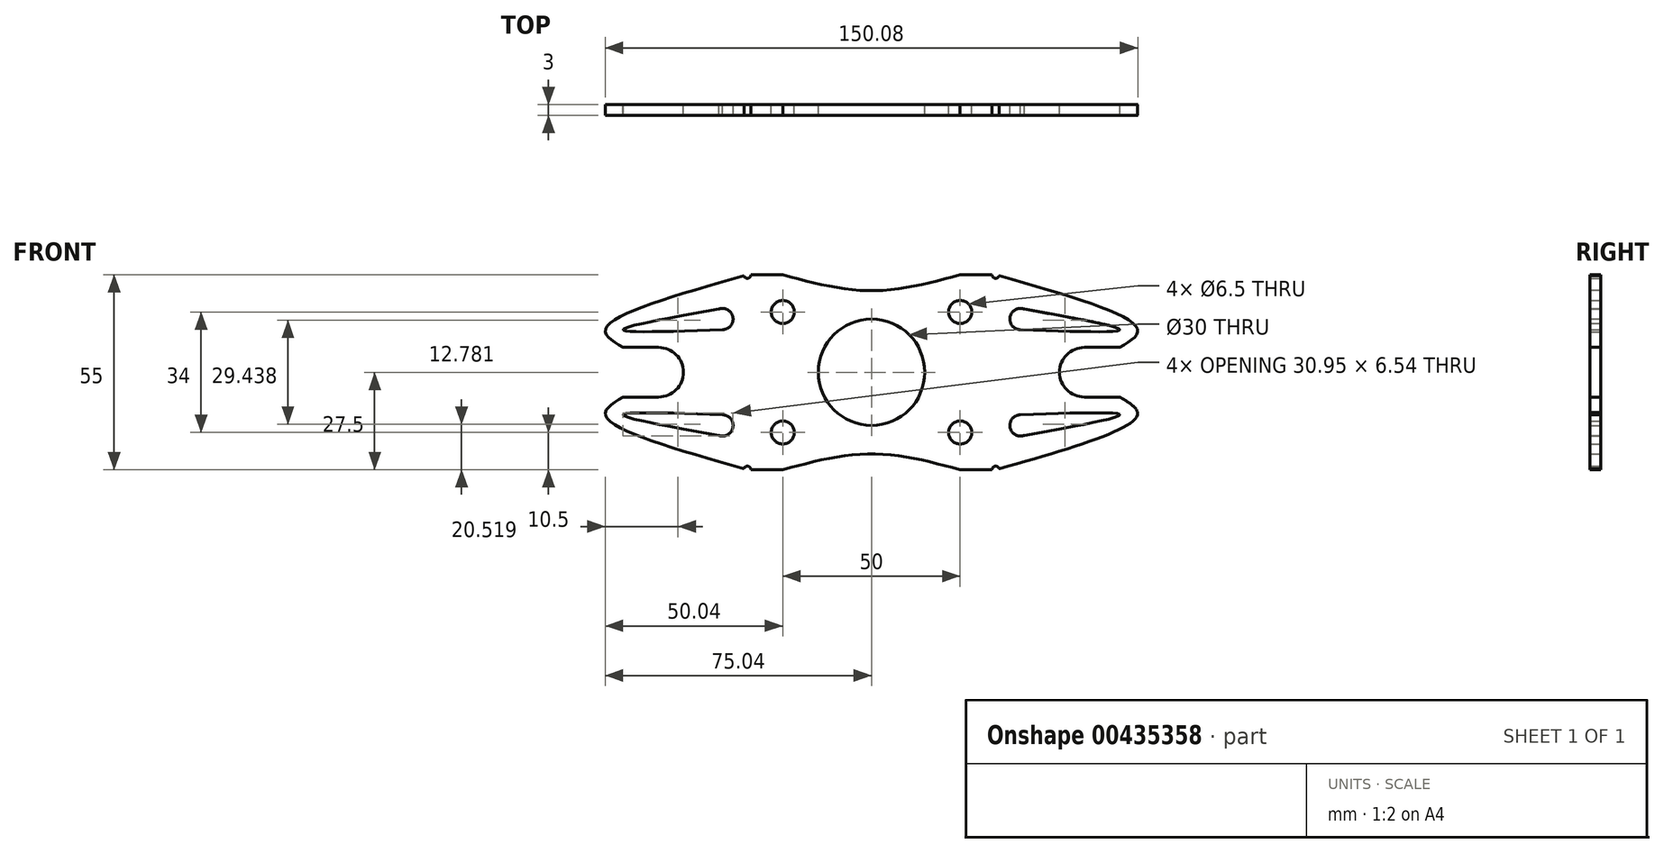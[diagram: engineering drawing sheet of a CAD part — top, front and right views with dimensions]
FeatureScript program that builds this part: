
annotation { "Feature Type Name" : "Feature", "Feature Type Description" : "" }
export const myFeature = defineFeature(function(context is Context, id is Id, definition is map)
    precondition{}
    {
        {
            var Q0;
            Q0=qCreatedBy(makeId("Front.planeOp"),FACE);
            var sketch = newSketch(context, id + "F0", { "sketchPlane" : qUnion([Q0])});
            skCircle(sketch, "E0", {"center": v(0, 0) * mm, "radius": 15 * mm});
            skLineSegment(sketch, "E1", {"start": v(-35, 26.5) * mm, "end": v(-35, 27.5) * mm});
            skLineSegment(sketch, "E2", {"start": v(-35, 27.5) * mm, "end": v(-35, 26.5) * mm});
            skLineSegment(sketch, "E3", {"start": v(-35, -27.5) * mm, "end": v(-25, -27.5) * mm});
            skLineSegment(sketch, "E4", {"start": v(35, -27.5) * mm, "end": v(35, -26.5) * mm});
            skLineSegment(sketch, "E5", {"start": v(35, 27.5) * mm, "end": v(25, 27.5) * mm});
            skLineSegment(sketch, "E6", {"start": v(25, 20.25) * mm, "end": v(25, 13.75) * mm});
            skLineSegment(sketch, "E7", {"start": v(-25, -20.25) * mm, "end": v(-25, -13.75) * mm});
            skLineSegment(sketch, "E8", {"start": v(25, 13.75) * mm, "end": v(25, 17) * mm});
            skLineSegment(sketch, "E9", {"start": v(25, 17) * mm, "end": v(25, 13.75) * mm});
            skArc(sketch, "E10", {"start": v(-60, -7) * mm, "mid": v(-53, 0) * mm, "end": v(-60, 7) * mm});
            skArc(sketch, "E11", {"start": v(60, 7) * mm, "mid": v(53, 0) * mm, "end": v(60, -7) * mm});
            skCircle(sketch, "E12", {"center": v(-25, 17) * mm, "radius": 3.25 * mm});
            skCircle(sketch, "E13", {"center": v(25, 17) * mm, "radius": 3.25 * mm});
            skCircle(sketch, "E14", {"center": v(25, -17) * mm, "radius": 3.25 * mm});
            skCircle(sketch, "E15", {"center": v(-25, -17) * mm, "radius": 3.25 * mm});
            skFitSpline(sketch, "E16", {"points": [v(-25, 27.5) * mm, v(0, 23) * mm, v(25, 27.5) * mm], "startDerivative": vector(50, -13.5) * mm, "endDerivative": vector(50, 13.5) * mm});
            skFitSpline(sketch, "E17", {"points": [v(-25, -27.5) * mm, v(0, -23) * mm, v(25, -27.5) * mm], "startDerivative": vector(50, 13.5) * mm, "endDerivative": vector(50, -13.5) * mm});
            skLineSegment(sketch, "E18", {"start": v(-60, -7) * mm, "end": v(-70, -7) * mm});
            skLineSegment(sketch, "E19", {"start": v(-60, 7) * mm, "end": v(-70, 7) * mm});
            skLineSegment(sketch, "E20", {"start": v(60, 7) * mm, "end": v(70, 7) * mm});
            skLineSegment(sketch, "E21", {"start": v(60, -7) * mm, "end": v(70, -7) * mm});
            skPoint(sketch, "E22.start.orphan", {"position": v(80, 7) * mm});
            skPoint(sketch, "E23.start.orphan", {"position": v(80, -7) * mm});
            skLineSegment(sketch, "E24.trimOffspring", {"start": v(25, -27.5) * mm, "end": v(35, -27.5) * mm});
            skLineSegment(sketch, "E25.trimOffspring", {"start": v(-25, 27.5) * mm, "end": v(-35, 27.5) * mm});
            skPoint(sketch, "E26.orphan", {"position": v(0, 27.5) * mm});
            skCircle(sketch, "E27", {"center": v(-35, 27.5) * mm, "radius": 1 * mm});
            skCircle(sketch, "E28", {"center": v(-35, -27.5) * mm, "radius": 1 * mm});
            skCircle(sketch, "E29", {"center": v(35, -27.5) * mm, "radius": 1 * mm});
            skCircle(sketch, "E30", {"center": v(35, 27.5) * mm, "radius": 1 * mm});
            skLineSegment(sketch, "E31.trimOffspring", {"start": v(-25, 13.75) * mm, "end": v(-25, 17) * mm});
            skPoint(sketch, "E32.start.orphan", {"position": v(-25, 0) * mm});
            skLineSegment(sketch, "E33.trimOffspring", {"start": v(35, 26.5) * mm, "end": v(35, 27.5) * mm});
            skPoint(sketch, "E34.orphan", {"position": v(35, 0) * mm});
            skLineSegment(sketch, "E35.trimOffspring", {"start": v(25, -13.75) * mm, "end": v(25, -17) * mm});
            skLineSegment(sketch, "E36.trimOffspring", {"start": v(25, -13.75) * mm, "end": v(25, -20.25) * mm});
            skPoint(sketch, "E37.orphan", {"position": v(25, 0) * mm});
            skLineSegment(sketch, "E38.trimOffspring", {"start": v(-25, -13.75) * mm, "end": v(-25, -17) * mm});
            skLineSegment(sketch, "E39.trimOffspring", {"start": v(-35, -26.5) * mm, "end": v(-35, -27.5) * mm});
            skLineSegment(sketch, "E40", {"start": v(35, 27.5) * mm, "end": v(35, 26.5) * mm});
            skPoint(sketch, "E41.newPointB", {"position": v(-35, -26.5) * mm});
            skPoint(sketch, "E42.end.orphan", {"position": v(75, -7) * mm});
            skLineSegment(sketch, "E43", {"start": v(75, -7) * mm, "end": v(75, -12) * mm});
            skFitSpline(sketch, "E44", {"points": [v(70, -7) * mm, v(75, -12) * mm, v(35, -27.5) * mm], "startDerivative": vector(27.94, -16.67) * mm, "endDerivative": vector(-82.4, -23.39) * mm});
            skLineSegment(sketch, "E45", {"start": v(42, -12) * mm, "end": v(42, -15) * mm});
            skCircle(sketch, "E46", {"center": v(42, -15) * mm, "radius": 3 * mm});
            skLineSegment(sketch, "E47", {"start": v(42, -15) * mm, "end": v(42, -18) * mm});
            skFitSpline(sketch, "E48", {"points": [v(42, -12) * mm, v(70, -12) * mm, v(42, -18) * mm], "startDerivative": vector(84.16, 2.97) * mm, "endDerivative": vector(-83.85, -14.93) * mm});
            skPoint(sketch, "E49.start.orphan", {"position": v(35, -12) * mm});
            skLineSegment(sketch, "E50", {"start": v(42, 12) * mm, "end": v(42, 15) * mm});
            skLineSegment(sketch, "E51", {"start": v(42, 15) * mm, "end": v(42, 18) * mm});
            skFitSpline(sketch, "E52", {"points": [v(35, 27.5) * mm, v(75, 12) * mm, v(70, 7) * mm], "startDerivative": vector(82.4, -23.39) * mm, "endDerivative": vector(-27.94, -16.67) * mm});
            skCircle(sketch, "E53", {"center": v(42, 15) * mm, "radius": 3 * mm});
            skFitSpline(sketch, "E54", {"points": [v(42, 18) * mm, v(70, 12) * mm, v(42, 12) * mm], "startDerivative": vector(83.85, -14.93) * mm, "endDerivative": vector(-84.16, 2.97) * mm});
            skPoint(sketch, "E55.end.orphan", {"position": v(42, 0) * mm});
            skLineSegment(sketch, "E56", {"start": v(-42, 12) * mm, "end": v(-42, 15) * mm});
            skLineSegment(sketch, "E57", {"start": v(-42, -12) * mm, "end": v(-42, -15) * mm});
            skCircle(sketch, "E58", {"center": v(-42, 15) * mm, "radius": 3 * mm});
            skCircle(sketch, "E59", {"center": v(-42, -15) * mm, "radius": 3 * mm});
            skLineSegment(sketch, "E60", {"start": v(-42, 12) * mm, "end": v(-42, 18) * mm});
            skLineSegment(sketch, "E61", {"start": v(-42, 18) * mm, "end": v(-42, 12) * mm});
            skFitSpline(sketch, "E62", {"points": [v(-70, 7) * mm, v(-75, 12) * mm, v(-35, 27.5) * mm], "startDerivative": vector(-27.94, 16.67) * mm, "endDerivative": vector(82.4, 23.39) * mm});
            skFitSpline(sketch, "E63", {"points": [v(-42, 12) * mm, v(-70, 12) * mm, v(-42, 18) * mm], "startDerivative": vector(-84.16, -2.97) * mm, "endDerivative": vector(83.85, 14.93) * mm});
            skLineSegment(sketch, "E64.trimOffspring", {"start": v(-42, -12) * mm, "end": v(-42, -18) * mm});
            skFitSpline(sketch, "E65", {"points": [v(-70, -7) * mm, v(-75, -12) * mm, v(-35, -27.5) * mm], "startDerivative": vector(-27.94, -16.67) * mm, "endDerivative": vector(82.4, -23.39) * mm});
            skFitSpline(sketch, "E66", {"points": [v(-42, -12) * mm, v(-70, -12) * mm, v(-42, -18) * mm], "startDerivative": vector(-84.16, 2.97) * mm, "endDerivative": vector(83.85, -14.93) * mm});
            skLineSegment(sketch, "E67", {"start": v(-35, 26.5) * mm, "end": v(-35, -26.5) * mm});
            skLineSegment(sketch, "E68", {"start": v(35, 26.5) * mm, "end": v(35, -26.5) * mm});
            skSolve(sketch);
        }
        {
            var Q0;
            Q0=makeQuery(id+"F0.imprint","IMPRINT",FACE,{"disambiguationData":[TD([[makeQuery(id+"F0.imprint","IMPRINT",EDGE,{"derivedFrom":sQuery(id+"F0.wireOp",EDGE,"E0")}),-1.0]])]});
            extrude(context, id + "F1", {"entities" : qUnion([Q0]), "depth" : 3 * mm, "offsetDistance" : 25 * mm});
        }
        {
            var Q0;
            Q0=makeQuery(id+"F0.imprint","IMPRINT",FACE,{"disambiguationData":[TD([[makeQuery(id+"F0.imprint","IMPRINT",EDGE,{"derivedFrom":sQuery(id+"F0.wireOp",EDGE,"E10")}),-1.0]])]});
            extrude(context, id + "F2", {"entities" : qUnion([Q0]), "operationType" : NewBodyOperationType.ADD, "depth" : 3 * mm, "offsetDistance" : 25 * mm});
        }
        {
            var Q0;
            Q0=makeQuery(id+"F0.imprint","IMPRINT",FACE,{"disambiguationData":[TD([[makeQuery(id+"F0.imprint","IMPRINT",EDGE,{"derivedFrom":sQuery(id+"F0.wireOp",EDGE,"E11")}),-1.0]])]});
            extrude(context, id + "F3", {"entities" : qUnion([Q0]), "operationType" : NewBodyOperationType.ADD, "depth" : 3 * mm, "offsetDistance" : 25 * mm});
        }
    });
